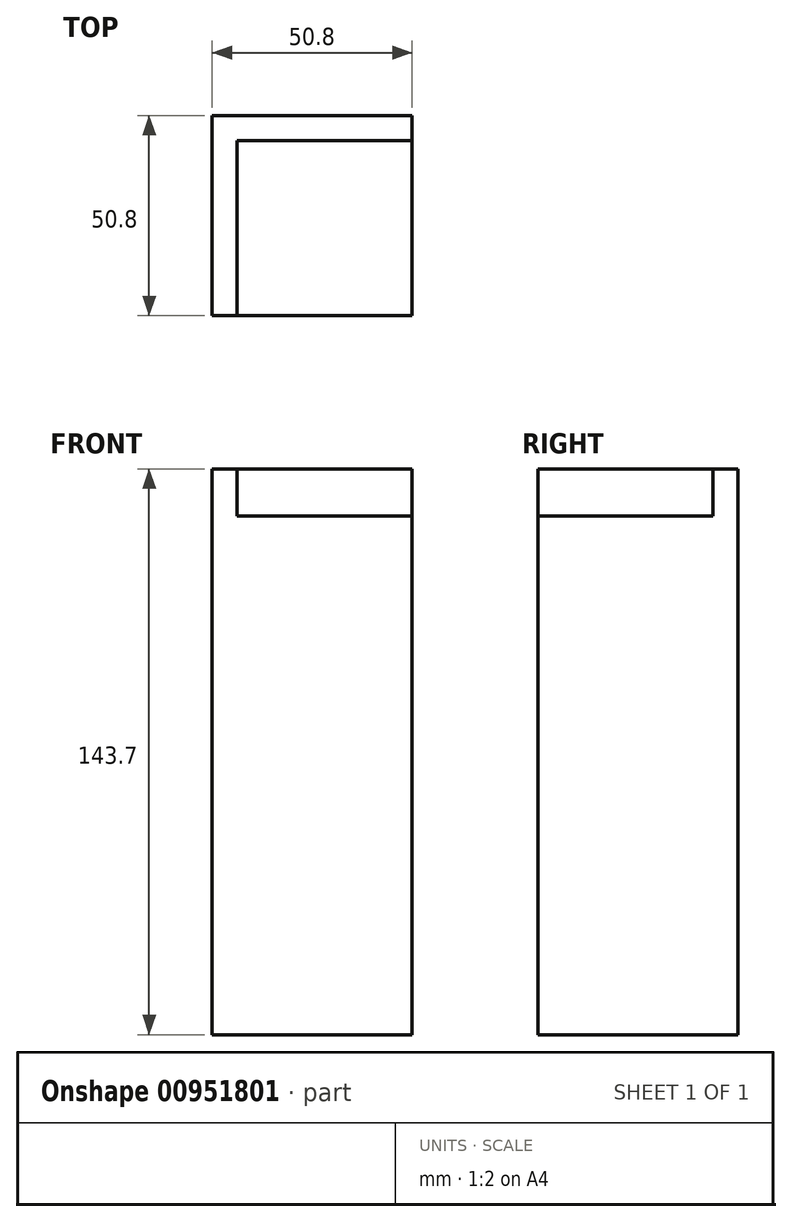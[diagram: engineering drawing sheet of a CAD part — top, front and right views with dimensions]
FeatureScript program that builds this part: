
annotation { "Feature Type Name" : "Feature", "Feature Type Description" : "" }
export const myFeature = defineFeature(function(context is Context, id is Id, definition is map)
    precondition{}
    {
        {
            var Q0;
            Q0=qCreatedBy(makeId("Front.planeOp"),FACE);
            var sketch = newSketch(context, id + "F0", { "sketchPlane" : qUnion([Q0])});
            skLineSegment(sketch, "E0.bottom", {"start": v(0, 0) * mm, "end": v(50.8, 0) * mm});
            skLineSegment(sketch, "E0.top", {"start": v(0, -131.76) * mm, "end": v(50.8, -131.76) * mm});
            skLineSegment(sketch, "E0.left", {"start": v(0, 0) * mm, "end": v(0, -131.76) * mm});
            skLineSegment(sketch, "E0.right", {"start": v(50.8, 0) * mm, "end": v(50.8, -131.76) * mm});
            skLineSegment(sketch, "E1.bottom", {"start": v(0, 0) * mm, "end": v(6.35, 0) * mm});
            skLineSegment(sketch, "E1.top", {"start": v(0, 11.94) * mm, "end": v(6.35, 11.94) * mm});
            skLineSegment(sketch, "E1.left", {"start": v(0, 0) * mm, "end": v(0, 11.94) * mm});
            skLineSegment(sketch, "E1.right", {"start": v(6.35, 0) * mm, "end": v(6.35, 11.94) * mm});
            skLineSegment(sketch, "E2.bottom", {"start": v(6.35, 11.94) * mm, "end": v(50.8, 11.94) * mm});
            skLineSegment(sketch, "E2.top", {"start": v(6.35, 0) * mm, "end": v(50.8, 0) * mm});
            skLineSegment(sketch, "E2.left", {"start": v(6.35, 11.94) * mm, "end": v(6.35, 0) * mm});
            skLineSegment(sketch, "E2.right", {"start": v(50.8, 11.94) * mm, "end": v(50.8, 0) * mm});
            skSolve(sketch);
        }
        {
            var Q0;
            Q0=makeQuery(id+"F0.imprint","IMPRINT",FACE,{"disambiguationData":[TD([[makeQuery(id+"F0.imprint","IMPRINT",EDGE,{"derivedFrom":sQuery(id+"F0.wireOp",EDGE,"E0.top")}),1.0]])]});
            extrude(context, id + "F1", {"entities" : qUnion([Q0]), "depth" : 50.8 * mm, "offsetDistance" : 25.4 * mm});
        }
        {
            var Q0;
            Q0=makeQuery(id+"F0.imprint","IMPRINT",FACE,{"disambiguationData":[TD([[makeQuery(id+"F0.imprint","IMPRINT",EDGE,{"derivedFrom":sQuery(id+"F0.wireOp",EDGE,"E1.top")}),-1.0]])]});
            var Q1;
            Q1=makeQuery(id+"F1.opExtrude","CAP_FACE",FACE,{"disambiguationData":[OSD([sQuery(id+"F0.wireOp",EDGE,"E0.bottom"),sQuery(id+"F0.wireOp",EDGE,"E0.top"),sQuery(id+"F0.wireOp",EDGE,"E0.left"),sQuery(id+"F0.wireOp",EDGE,"E0.right")])],"isStart":false});
            extrude(context, id + "F2", {"entities" : qUnion([Q0]), "operationType" : NewBodyOperationType.ADD, "endBound" : BoundingType.UP_TO_SURFACE, "depth" : 25.4 * mm, "endBoundEntityFace" : qUnion([Q1]), "offsetDistance" : 25.4 * mm});
        }
        {
            var Q0;
            {var subQ0=sQuery(id+"F0.wireOp",EDGE,"E1.right");Q0=makeQuery(id+"F0.imprint","IMPRINT",FACE,{"disambiguationData":[TD([[makeQuery(id+"F0.imprint","IMPRINT",EDGE,{"derivedFrom":subQ0}),-1.0]])]});}
            extrude(context, id + "F3", {"entities" : qUnion([Q0]), "operationType" : NewBodyOperationType.ADD, "depth" : 6.35 * mm, "offsetDistance" : 25.4 * mm});
        }
    });
